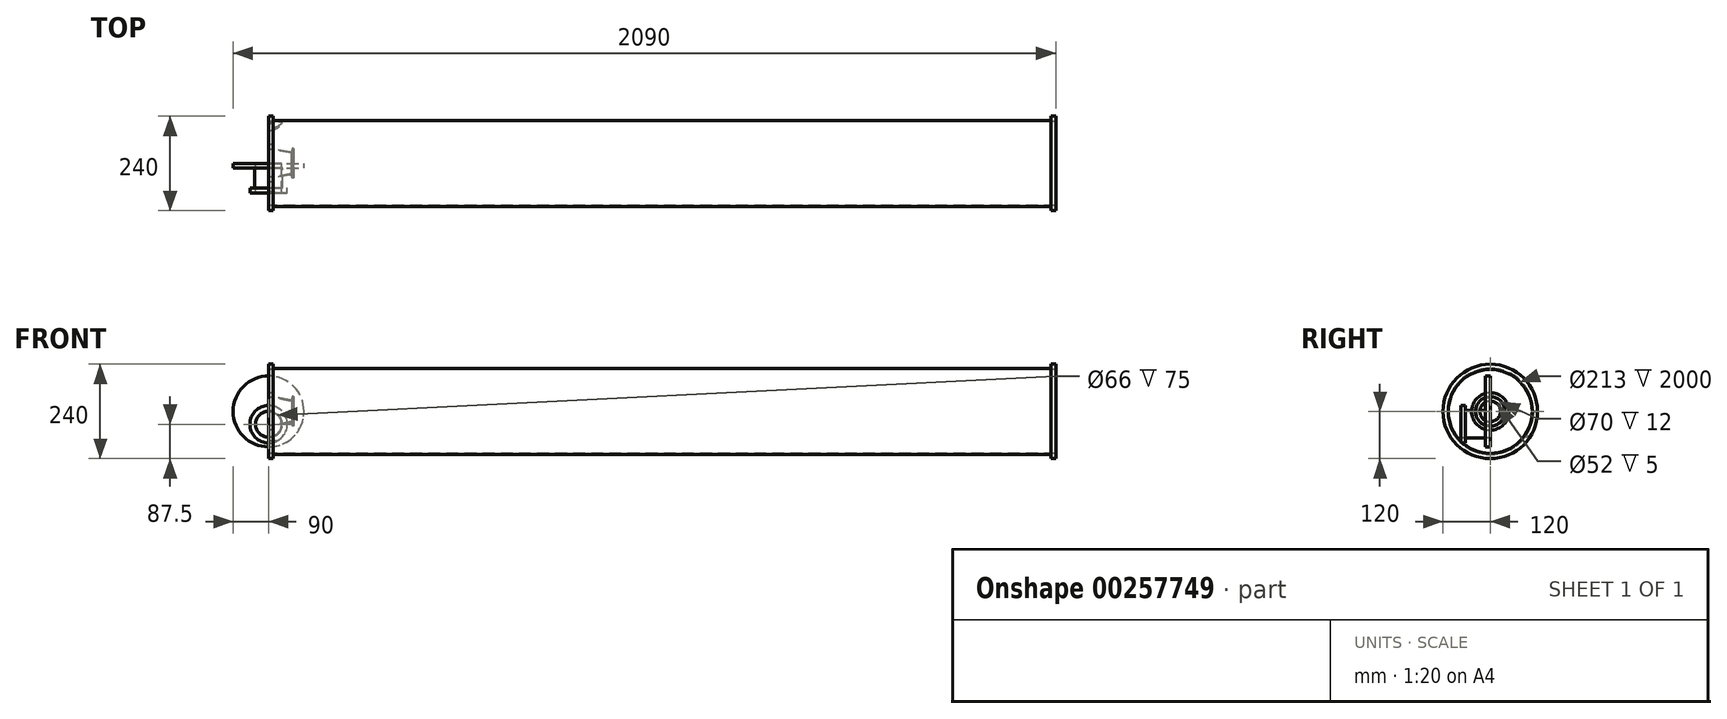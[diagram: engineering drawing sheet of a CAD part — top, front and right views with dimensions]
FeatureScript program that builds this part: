
annotation { "Feature Type Name" : "Feature", "Feature Type Description" : "" }
export const myFeature = defineFeature(function(context is Context, id is Id, definition is map)
    precondition{}
    {
        {
            var Q0;
            Q0=qCreatedBy(makeId("Front.planeOp"),FACE);
            var sketch = newSketch(context, id + "F0", { "sketchPlane" : qUnion([Q0])});
            skLineSegment(sketch, "E0", {"start": v(0, 106.5) * mm, "end": v(0, 120) * mm});
            skLineSegment(sketch, "E1", {"start": v(0, 120) * mm, "end": v(12, 120) * mm});
            skLineSegment(sketch, "E2", {"start": v(12, 120) * mm, "end": v(12, 109.5) * mm});
            skLineSegment(sketch, "E3", {"start": v(12, 109.5) * mm, "end": v(1988, 109.5) * mm});
            skLineSegment(sketch, "E4", {"start": v(1988, 109.5) * mm, "end": v(1988, 120) * mm});
            skLineSegment(sketch, "E5", {"start": v(1988, 120) * mm, "end": v(2000, 120) * mm});
            skLineSegment(sketch, "E6", {"start": v(2000, 120) * mm, "end": v(2000, 106.5) * mm});
            skLineSegment(sketch, "E7", {"start": v(2000, 106.5) * mm, "end": v(0, 106.5) * mm});
            skSolve(sketch);
        }
        {
            var Q0;
            Q0=qCreatedBy(makeId("Front.planeOp"),FACE);
            var sketch = newSketch(context, id + "F1", { "sketchPlane" : qUnion([Q0])});
            skLineSegment(sketch, "E8", {"start": v(0, 0) * mm, "end": v(91.38, 0) * mm, "construction": true});
            skSolve(sketch);
        }
        {
            var Q0;
            Q0 = qSketchRegion(id + "F0", true);
            var Q1;
            Q1=sQuery(id+"F1.wireOp",EDGE,"E8");
            revolve(context, id + "F2", {"entities" : qUnion([Q0]), "axis" : qUnion([Q1]), "revolveType" : RevolveType.FULL});
        }
        {
            var Q0;
            Q0=qCreatedBy(makeId("Front.planeOp"),FACE);
            var sketch = newSketch(context, id + "F3", { "sketchPlane" : qUnion([Q0])});
            skCircle(sketch, "E9", {"center": v(0, 0) * mm, "radius": 90 * mm});
            skSolve(sketch);
        }
        {
            var Q0;
            Q0=makeQuery(id+"F3.imprint","IMPRINT",FACE,{"disambiguationData":[TD([[makeQuery(id+"F3.imprint","IMPRINT",EDGE,{"derivedFrom":sQuery(id+"F3.wireOp",EDGE,"E9")}),1.0]])]});
            extrude(context, id + "F4", {"entities" : qUnion([Q0]), "depth" : 12 * mm});
        }
        {
            var Q0;
            Q0=makeQuery(id+"F4.opExtrude","CAP_FACE",FACE,{"disambiguationData":[OSD([sQuery(id+"F3.wireOp",EDGE,"E9")])],"isStart":false});
            var sketch = newSketch(context, id + "F5", { "sketchPlane" : qUnion([Q0])});
            skCircle(sketch, "E10", {"center": v(0, -32.5) * mm, "radius": 35 * mm});
            skCircle(sketch, "E11", {"center": v(0, -32.5) * mm, "radius": 33 * mm});
            skSolve(sketch);
        }
        {
            var Q0;
            Q0=makeQuery(id+"F5.imprint","IMPRINT",FACE,{"disambiguationData":[TD([[makeQuery(id+"F5.imprint","IMPRINT",EDGE,{"derivedFrom":sQuery(id+"F5.wireOp",EDGE,"E10")}),1.0]])]});
            extrude(context, id + "F6", {"entities" : qUnion([Q0]), "operationType" : NewBodyOperationType.ADD, "depth" : 51 * mm});
        }
        {
            var Q0;
            Q0=makeQuery(id+"F5.imprint","IMPRINT",FACE,{"disambiguationData":[TD([[makeQuery(id+"F5.imprint","IMPRINT",EDGE,{"derivedFrom":sQuery(id+"F5.wireOp",EDGE,"E11")}),1.0]])]});
            extrude(context, id + "F7", {"entities" : qUnion([Q0]), "operationType" : NewBodyOperationType.REMOVE, "endBound" : BoundingType.THROUGH_ALL, "oppositeDirection" : true, "depth" : 25 * mm});
        }
        {
            var Q0;
            Q0=makeQuery(id+"F6.opExtrude","CAP_FACE",FACE,{"disambiguationData":[OSD([sQuery(id+"F5.wireOp",EDGE,"E10"),sQuery(id+"F5.wireOp",EDGE,"E11")])],"isStart":false});
            var sketch = newSketch(context, id + "F8", { "sketchPlane" : qUnion([Q0])});
            skCircle(sketch, "E12.0", {"center": v(0, -32.5) * mm, "radius": 47.5 * mm});
            skSolve(sketch);
        }
        {
            var Q0;
            Q0=makeQuery(id+"F8.imprint","IMPRINT",FACE,{"disambiguationData":[TD([[makeQuery(id+"F8.imprint","IMPRINT",EDGE,{"derivedFrom":sQuery(id+"F8.wireOp",EDGE,"E12.0")}),1.0]])]});
            var Q1;
            Q1=makeQuery(id+"F8.imprint","IMPRINT",FACE,{"disambiguationData":[TD([[makeQuery(id+"F8.imprint","IMPRINT",EDGE,{"derivedFrom":makeQuery(id+"F6.opExtrude","CAP_EDGE",EDGE,{"disambiguationData":[OSD([sQuery(id+"F5.wireOp",EDGE,"E10")])],"isStart":false})}),1.0]])]});
            extrude(context, id + "F9", {"entities" : qUnion([Q0, Q1]), "operationType" : NewBodyOperationType.ADD, "depth" : 12 * mm});
        }
        {
            var Q0;
            Q0=qCreatedBy(makeId("Front.planeOp"),FACE);
            var sketch = newSketch(context, id + "F10", { "sketchPlane" : qUnion([Q0])});
            skLineSegment(sketch, "E13", {"start": v(0, 35) * mm, "end": v(0, 47.5) * mm});
            skLineSegment(sketch, "E14", {"start": v(0, 47.5) * mm, "end": v(12, 47.5) * mm});
            skLineSegment(sketch, "E15", {"start": v(12, 47.5) * mm, "end": v(12, 37.04) * mm});
            skLineSegment(sketch, "E16", {"start": v(12, 37.04) * mm, "end": v(54.04, 28.81) * mm});
            skLineSegment(sketch, "E17", {"start": v(60, 33.72) * mm, "end": v(60, 37.5) * mm});
            skLineSegment(sketch, "E18", {"start": v(60, 37.5) * mm, "end": v(63, 37.5) * mm});
            skLineSegment(sketch, "E19", {"start": v(63, 37.5) * mm, "end": v(63, 26) * mm});
            skLineSegment(sketch, "E20", {"start": v(63, 26) * mm, "end": v(58, 26) * mm});
            skLineSegment(sketch, "E21", {"start": v(58, 26) * mm, "end": v(12, 35) * mm});
            skLineSegment(sketch, "E22", {"start": v(12, 35) * mm, "end": v(0, 35) * mm});
            skPoint(sketch, "E23.visualSharp", {"position": v(60, 27.65) * mm});
            skArc(sketch, "E23.filletArc", {"start": v(54.04, 28.81) * mm, "mid": v(58.18, 29.86) * mm, "end": v(60, 33.72) * mm});
            skSolve(sketch);
        }
        {
            var Q0;
            Q0=qCreatedBy(makeId("Front.planeOp"),FACE);
            var sketch = newSketch(context, id + "F11", { "sketchPlane" : qUnion([Q0])});
            skLineSegment(sketch, "E24", {"start": v(0, 0) * mm, "end": v(67.77, 0) * mm, "construction": true});
            skSolve(sketch);
        }
        {
            var Q0;
            Q0=makeQuery(id+"F10.imprint","IMPRINT",FACE,{"disambiguationData":[TD([[makeQuery(id+"F10.imprint","IMPRINT",EDGE,{"derivedFrom":sQuery(id+"F10.wireOp",EDGE,"E13")}),-1.0]])]});
            var Q1;
            Q1=sQuery(id+"F11.wireOp",EDGE,"E24");
            revolve(context, id + "F12", {"entities" : qUnion([Q0]), "axis" : qUnion([Q1]), "revolveType" : RevolveType.FULL});
        }
    });
